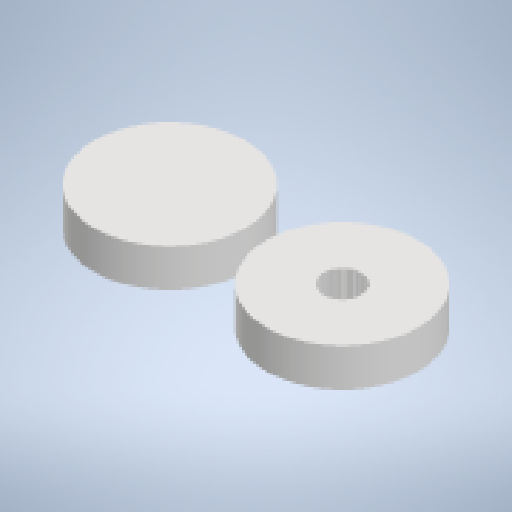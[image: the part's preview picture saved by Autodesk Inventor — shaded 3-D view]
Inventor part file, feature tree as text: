
AUTODESK INVENTOR PART (.ipt)
format: ipt  version: 2024 (Build 280153000, 153)  size: 555,520 bytes
history: native  units: mm
features: reference x225, other x5, extrude x2, sketch x2
ambient origin geometry x8: Origin, YZ Plane, XZ Plane, XY Plane, X Axis, Y Axis, Z Axis, Center Point
bodies: Solid1 (feature_tree)
feature tree (234):
  extrude  "Extrusion1"  Depth=2.497998mm
  extrude  "Extrusion2"  Depth=5.0mm
  sketch  "Sketch1"  dims[d0=0.05mm d1=2.497998mm]
  reference  "Reference1"
  reference  "Reference2"
  reference  "Reference3"
  reference  "Reference4"
  reference  "Reference5"
  reference  "Reference6"
  reference  "Reference7"
  reference  "Reference8"
  reference  "Reference9"
  reference  "Reference10"
  reference  "Reference11"
  reference  "Reference12"
  reference  "Reference13"
  reference  "Reference14"
  reference  "Reference15"
  reference  "Reference16"
  reference  "Reference17"
  reference  "Reference18"
  reference  "Reference19"
  reference  "Reference20"
  reference  "Reference21"
  reference  "Reference22"
  reference  "Reference23"
  reference  "Reference24"
  reference  "Reference25"
  reference  "Reference26"
  reference  "Reference27"
  reference  "Reference28"
  reference  "Reference29"
  reference  "Reference30"
  reference  "Reference31"
  reference  "Reference32"
  reference  "Reference33"
  reference  "Reference34"
  reference  "Reference35"
  reference  "Reference36"
  reference  "Reference37"
  reference  "Reference38"
  reference  "Reference39"
  reference  "Reference40"
  reference  "Reference41"
  reference  "Reference42"
  reference  "Reference43"
  reference  "Reference44"
  reference  "Reference45"
  reference  "Reference46"
  reference  "Reference47"
  reference  "Reference48"
  reference  "Reference49"
  reference  "Reference50"
  reference  "Reference51"
  reference  "Reference52"
  reference  "Reference53"
  reference  "Reference54"
  reference  "Reference55"
  reference  "Reference56"
  reference  "Reference57"
  reference  "Reference58"
  reference  "Reference59"
  reference  "Reference60"
  reference  "Reference61"
  reference  "Reference62"
  reference  "Reference63"
  reference  "Reference64"
  reference  "Reference65"
  reference  "Reference66"
  reference  "Reference67"
  reference  "Reference68"
  reference  "Reference69"
  reference  "Reference70"
  reference  "Reference71"
  reference  "Reference72"
  reference  "Reference73"
  reference  "Reference74"
  reference  "Reference75"
  reference  "Reference76"
  reference  "Reference77"
  reference  "Reference78"
  reference  "Reference79"
  reference  "Reference80"
  reference  "Reference81"
  reference  "Reference82"
  reference  "Reference83"
  reference  "Reference84"
  reference  "Reference85"
  reference  "Reference86"
  reference  "Reference87"
  reference  "Reference88"
  reference  "Reference89"
  reference  "Reference90"
  reference  "Reference91"
  reference  "Reference92"
  reference  "Reference93"
  reference  "Reference94"
  reference  "Reference95"
  reference  "Reference96"
  reference  "Reference97"
  reference  "Reference98"
  reference  "Reference99"
  reference  "Reference100"
  reference  "Reference101"
  reference  "Reference102"
  reference  "Reference103"
  reference  "Reference104"
  reference  "Reference105"
  reference  "Reference106"
  reference  "Reference107"
  reference  "Reference108"
  reference  "Reference109"
  reference  "Reference110"
  reference  "Reference111"
  reference  "Reference112"
  reference  "Reference113"
  reference  "Reference114"
  reference  "Reference115"
  reference  "Reference116"
  reference  "Reference117"
  reference  "Reference118"
  reference  "Reference119"
  reference  "Reference120"
  reference  "Reference121"
  reference  "Reference122"
  reference  "Reference123"
  reference  "Reference124"
  reference  "Reference125"
  reference  "Reference126"
  reference  "Reference127"
  reference  "Reference128"
  reference  "Reference129"
  reference  "Reference130"
  reference  "Reference131"
  reference  "Reference132"
  reference  "Reference133"
  reference  "Reference134"
  reference  "Reference135"
  reference  "Reference136"
  reference  "Reference137"
  reference  "Reference138"
  reference  "Reference139"
  reference  "Reference140"
  reference  "Reference141"
  reference  "Reference142"
  reference  "Reference143"
  reference  "Reference144"
  reference  "Reference145"
  reference  "Reference146"
  reference  "Reference147"
  reference  "Reference148"
  reference  "Reference149"
  reference  "Reference150"
  reference  "Reference151"
  reference  "Reference152"
  reference  "Reference153"
  reference  "Reference154"
  reference  "Reference155"
  reference  "Reference156"
  reference  "Reference157"
  reference  "Reference158"
  reference  "Reference159"
  reference  "Reference160"
  reference  "Reference161"
  reference  "Reference162"
  reference  "Reference163"
  reference  "Reference164"
  reference  "Reference165"
  reference  "Reference166"
  reference  "Reference167"
  reference  "Reference168"
  reference  "Reference169"
  reference  "Reference170"
  reference  "Reference171"
  reference  "Reference172"
  reference  "Reference173"
  reference  "Reference174"
  reference  "Reference175"
  reference  "Reference176"
  reference  "Reference177"
  reference  "Reference178"
  reference  "Reference179"
  reference  "Reference180"
  reference  "Reference181"
  reference  "Reference182"
  reference  "Reference183"
  reference  "Reference184"
  reference  "Reference185"
  reference  "Reference186"
  reference  "Reference187"
  reference  "Reference188"
  reference  "Reference189"
  reference  "Reference190"
  reference  "Reference191"
  reference  "Reference192"
  reference  "Reference193"
  reference  "Reference194"
  reference  "Reference195"
  reference  "Reference196"
  reference  "Reference197"
  reference  "Reference198"
  reference  "Reference199"
  reference  "Reference200"
  reference  "Reference202"
  reference  "Reference203"
  reference  "Reference204"
  reference  "Reference205"
  reference  "Reference206"
  reference  "Reference207"
  reference  "Reference208"
  reference  "Reference209"
  reference  "Reference210"
  reference  "Reference211"
  reference  "Reference212"
  reference  "Reference213"
  reference  "Reference214"
  reference  "Reference215"
  reference  "Reference216"
  reference  "Reference217"
  reference  "Reference218"
  reference  "Reference219"
  reference  "Reference220"
  reference  "Reference221"
  reference  "Reference222"
  reference  "Reference223"
  reference  "Reference224"
  reference  "Reference225"
  reference  "Reference226"
  sketch  "Sketch2"  dims[d2=1.749007mm d3=0.05mm d4=2.385355mm d5=1.789435mm d6=0.05mm d7=0.05mm d8=20.0mm d9=5.0mm d10=0.0mm d12=20.0mm d13=5.0mm d14=0.0mm]
  other  "<userpath> windows\Documents\Inventor\Robotska_roka\Assembly4.iam"
  other  "Assembly4.iam"
  other  "SG90 - Micro Servo 9g - Tower Pro:3"
  other  "Tower Pro - Micro Servo 9g - SG90.1_12"
  other  "Tower Pro - Micro Servo 9g - SG90.1_11"
